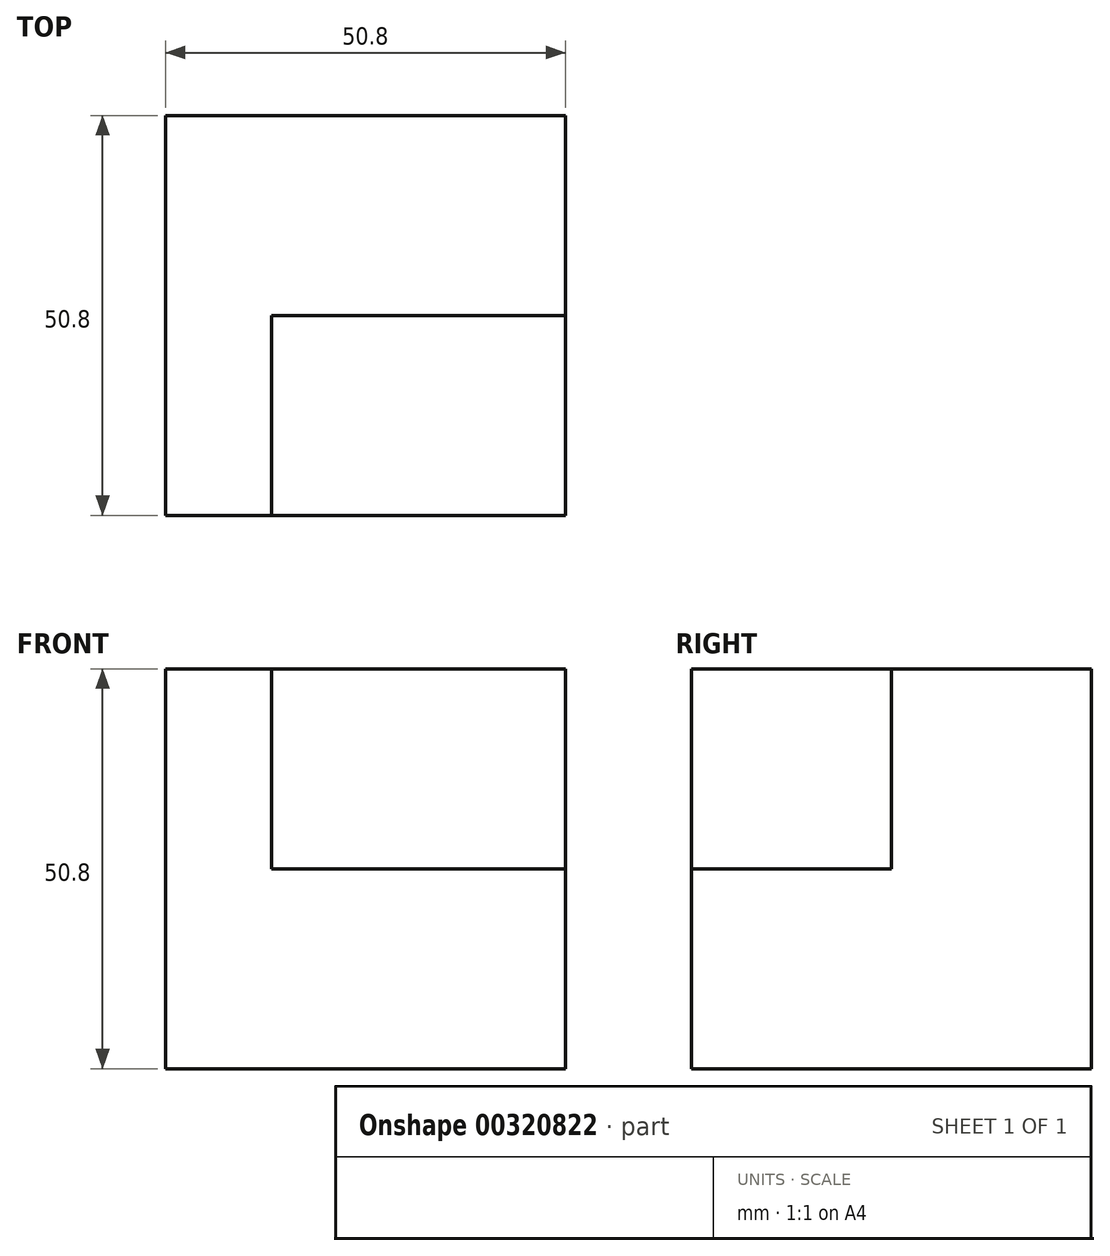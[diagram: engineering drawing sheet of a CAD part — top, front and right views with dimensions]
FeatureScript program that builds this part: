
annotation { "Feature Type Name" : "Feature", "Feature Type Description" : "" }
export const myFeature = defineFeature(function(context is Context, id is Id, definition is map)
    precondition{}
    {
        {
            var Q0;
            Q0=qCreatedBy(makeId("Front.planeOp"),FACE);
            var sketch = newSketch(context, id + "F0", { "sketchPlane" : qUnion([Q0])});
            skLineSegment(sketch, "E0", {"start": v(-34.97, 26.34) * mm, "end": v(-34.97, -24.46) * mm});
            skLineSegment(sketch, "E1", {"start": v(-34.97, -24.46) * mm, "end": v(15.83, -24.46) * mm});
            skLineSegment(sketch, "E2", {"start": v(15.83, -24.46) * mm, "end": v(15.83, 26.34) * mm});
            skLineSegment(sketch, "E3", {"start": v(15.83, 26.34) * mm, "end": v(-34.97, 26.34) * mm});
            skSolve(sketch);
        }
        {
            var Q0;
            Q0=makeQuery(id+"F0.imprint","IMPRINT",FACE,{"disambiguationData":[TD([[makeQuery(id+"F0.imprint","IMPRINT",EDGE,{"derivedFrom":sQuery(id+"F0.wireOp",EDGE,"E0")}),1.0]])]});
            extrude(context, id + "F1", {"entities" : qUnion([Q0]), "oppositeDirection" : true, "depth" : 50.8 * mm});
        }
        {
            var Q0;
            Q0=makeQuery(id+"F1.opExtrude","CAP_FACE",FACE,{"disambiguationData":[OSD([sQuery(id+"F0.wireOp",EDGE,"E0"),sQuery(id+"F0.wireOp",EDGE,"E1"),sQuery(id+"F0.wireOp",EDGE,"E2"),sQuery(id+"F0.wireOp",EDGE,"E3")])],"isStart":true});
            var sketch = newSketch(context, id + "F2", { "sketchPlane" : qUnion([Q0])});
            skLineSegment(sketch, "E4", {"start": v(-34.97, 26.34) * mm, "end": v(-21.5, 26.34) * mm});
            skLineSegment(sketch, "E5", {"start": v(-21.5, 26.34) * mm, "end": v(-21.5, 0.94) * mm});
            skLineSegment(sketch, "E6", {"start": v(-21.5, 0.94) * mm, "end": v(16.6, 0.94) * mm});
            skLineSegment(sketch, "E7", {"start": v(16.6, 0.94) * mm, "end": v(16.6, 26.34) * mm});
            skLineSegment(sketch, "E8", {"start": v(16.6, 26.34) * mm, "end": v(-21.5, 26.34) * mm});
            skSolve(sketch);
        }
        {
            var Q0;
            {var subQ0=sQuery(id+"F2.wireOp",EDGE,"E5");Q0=makeQuery(id+"F2.imprint","IMPRINT",FACE,{"disambiguationData":[TD([[makeQuery(id+"F2.imprint","IMPRINT",EDGE,{"derivedFrom":subQ0}),1.0]])]});}
            extrude(context, id + "F3", {"entities" : qUnion([Q0]), "operationType" : NewBodyOperationType.REMOVE, "oppositeDirection" : true, "depth" : 25.4 * mm});
        }
    });
